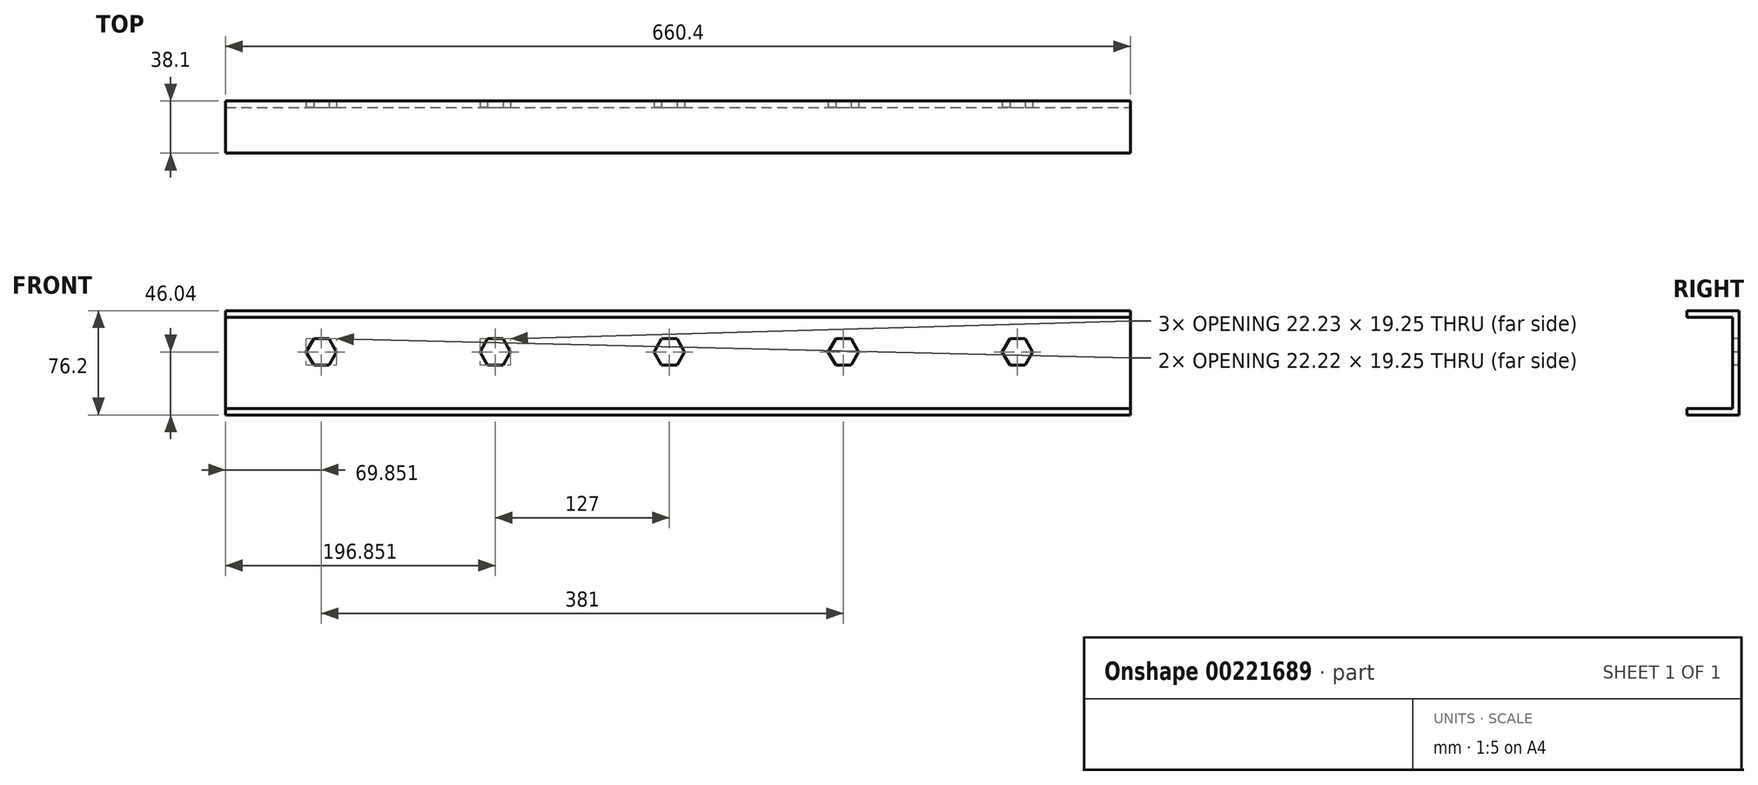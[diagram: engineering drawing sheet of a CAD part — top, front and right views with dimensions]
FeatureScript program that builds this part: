
annotation { "Feature Type Name" : "Feature", "Feature Type Description" : "" }
export const myFeature = defineFeature(function(context is Context, id is Id, definition is map)
    precondition{}
    {
        {
            var Q0;
            Q0=qCreatedBy(makeId("Front.planeOp"),FACE);
            var sketch = newSketch(context, id + "F0", { "sketchPlane" : qUnion([Q0])});
            skLineSegment(sketch, "E0.bottom", {"start": v(-341.97, -48.15) * mm, "end": v(318.43, -48.15) * mm});
            skLineSegment(sketch, "E0.top", {"start": v(-341.97, 28.05) * mm, "end": v(318.43, 28.05) * mm});
            skLineSegment(sketch, "E0.left", {"start": v(-341.97, -48.15) * mm, "end": v(-341.97, 28.05) * mm});
            skLineSegment(sketch, "E0.right", {"start": v(318.43, -48.15) * mm, "end": v(318.43, 28.05) * mm});
            skSolve(sketch);
        }
        {
            var Q0;
            Q0 = qSketchRegion(id + "F0", true);
            extrude(context, id + "F1", {"entities" : qUnion([Q0]), "oppositeDirection" : true, "depth" : 38.1 * mm});
        }
        {
            var Q0;
            Q0=makeQuery(id+"F1.opExtrude","CAP_FACE",FACE,{"disambiguationData":[OSD([sQuery(id+"F0.wireOp",EDGE,"E0.bottom"),sQuery(id+"F0.wireOp",EDGE,"E0.top"),sQuery(id+"F0.wireOp",EDGE,"E0.left"),sQuery(id+"F0.wireOp",EDGE,"E0.right")])],"isStart":true});
            var sketch = newSketch(context, id + "F2", { "sketchPlane" : qUnion([Q0])});
            skLineSegment(sketch, "E1.bottom", {"start": v(-341.97, -43.38) * mm, "end": v(318.43, -43.38) * mm});
            skLineSegment(sketch, "E1.top", {"start": v(-341.97, 23.3) * mm, "end": v(318.43, 23.3) * mm});
            skLineSegment(sketch, "E1.left", {"start": v(-341.97, -43.38) * mm, "end": v(-341.97, 23.3) * mm});
            skLineSegment(sketch, "E1.right", {"start": v(318.43, -43.38) * mm, "end": v(318.43, 23.3) * mm});
            skSolve(sketch);
        }
        {
            var Q0;
            Q0 = qSketchRegion(id + "F2", true);
            extrude(context, id + "F3", {"entities" : qUnion([Q0]), "operationType" : NewBodyOperationType.REMOVE, "oppositeDirection" : true, "depth" : 33.34 * mm});
        }
        {
            var Q0;
            Q0=makeQuery(id+"F3.boolean.opBoolean","COPY",FACE,{"derivedFrom":makeQuery(id+"F3.opExtrude","CAP_FACE",FACE,{"disambiguationData":[OSD([sQuery(id+"F2.wireOp",EDGE,"E1.bottom"),sQuery(id+"F2.wireOp",EDGE,"E1.top"),sQuery(id+"F2.wireOp",EDGE,"E1.left"),sQuery(id+"F2.wireOp",EDGE,"E1.right")])],"isStart":false})});
            var sketch = newSketch(context, id + "F4", { "sketchPlane" : qUnion([Q0])});
            skCircle(sketch, "E2.cCircle", {"center": v(-272.12, -2.1) * mm, "radius": 9.62 * mm, "construction": true});
            skLineSegment(sketch, "E2.0", {"start": v(-283.23, -2.1) * mm, "end": v(-277.68, 7.51) * mm});
            skLineSegment(sketch, "E2.1", {"start": v(-277.68, 7.51) * mm, "end": v(-266.56, 7.51) * mm});
            skLineSegment(sketch, "E2.2", {"start": v(-266.56, 7.51) * mm, "end": v(-261, -2.1) * mm});
            skLineSegment(sketch, "E2.3", {"start": v(-261, -2.1) * mm, "end": v(-266.56, -11.73) * mm});
            skLineSegment(sketch, "E2.4", {"start": v(-266.56, -11.73) * mm, "end": v(-277.68, -11.73) * mm});
            skLineSegment(sketch, "E2.5", {"start": v(-277.68, -11.73) * mm, "end": v(-283.23, -2.1) * mm});
            skPoint(sketch, "E2.0.midPoint", {"position": v(-280.45, 2.7) * mm});
            skCircle(sketch, "E3.1.0.0", {"center": v(-145.12, -2.1) * mm, "radius": 9.62 * mm, "construction": true});
            skLineSegment(sketch, "E3.1.0.1", {"start": v(-156.23, -2.1) * mm, "end": v(-150.68, 7.51) * mm});
            skLineSegment(sketch, "E3.1.0.2", {"start": v(-150.68, -11.73) * mm, "end": v(-156.23, -2.1) * mm});
            skLineSegment(sketch, "E3.1.0.3", {"start": v(-139.56, -11.73) * mm, "end": v(-150.68, -11.73) * mm});
            skLineSegment(sketch, "E3.1.0.4", {"start": v(-134, -2.1) * mm, "end": v(-139.56, -11.73) * mm});
            skLineSegment(sketch, "E3.1.0.5", {"start": v(-139.56, 7.51) * mm, "end": v(-134, -2.1) * mm});
            skLineSegment(sketch, "E3.1.0.6", {"start": v(-150.68, 7.51) * mm, "end": v(-139.56, 7.51) * mm});
            skCircle(sketch, "E3.2.0.0", {"center": v(-18.12, -2.1) * mm, "radius": 9.62 * mm, "construction": true});
            skLineSegment(sketch, "E3.2.0.1", {"start": v(-29.23, -2.1) * mm, "end": v(-23.68, 7.51) * mm});
            skLineSegment(sketch, "E3.2.0.2", {"start": v(-23.68, -11.73) * mm, "end": v(-29.23, -2.1) * mm});
            skLineSegment(sketch, "E3.2.0.3", {"start": v(-12.56, -11.73) * mm, "end": v(-23.68, -11.73) * mm});
            skLineSegment(sketch, "E3.2.0.4", {"start": v(-7, -2.1) * mm, "end": v(-12.56, -11.73) * mm});
            skLineSegment(sketch, "E3.2.0.5", {"start": v(-12.56, 7.51) * mm, "end": v(-7, -2.1) * mm});
            skLineSegment(sketch, "E3.2.0.6", {"start": v(-23.68, 7.51) * mm, "end": v(-12.56, 7.51) * mm});
            skCircle(sketch, "E3.3.0.0", {"center": v(108.88, -2.1) * mm, "radius": 9.62 * mm, "construction": true});
            skLineSegment(sketch, "E3.3.0.1", {"start": v(97.77, -2.1) * mm, "end": v(103.32, 7.51) * mm});
            skLineSegment(sketch, "E3.3.0.2", {"start": v(103.32, -11.73) * mm, "end": v(97.77, -2.1) * mm});
            skLineSegment(sketch, "E3.3.0.3", {"start": v(114.44, -11.73) * mm, "end": v(103.32, -11.73) * mm});
            skLineSegment(sketch, "E3.3.0.4", {"start": v(120, -2.1) * mm, "end": v(114.44, -11.73) * mm});
            skLineSegment(sketch, "E3.3.0.5", {"start": v(114.44, 7.51) * mm, "end": v(120, -2.1) * mm});
            skLineSegment(sketch, "E3.3.0.6", {"start": v(103.32, 7.51) * mm, "end": v(114.44, 7.51) * mm});
            skCircle(sketch, "E3.4.0.0", {"center": v(235.88, -2.1) * mm, "radius": 9.62 * mm, "construction": true});
            skLineSegment(sketch, "E3.4.0.1", {"start": v(224.77, -2.1) * mm, "end": v(230.32, 7.51) * mm});
            skLineSegment(sketch, "E3.4.0.2", {"start": v(230.32, -11.73) * mm, "end": v(224.77, -2.1) * mm});
            skLineSegment(sketch, "E3.4.0.3", {"start": v(241.44, -11.73) * mm, "end": v(230.32, -11.73) * mm});
            skLineSegment(sketch, "E3.4.0.4", {"start": v(247, -2.1) * mm, "end": v(241.44, -11.73) * mm});
            skLineSegment(sketch, "E3.4.0.5", {"start": v(241.44, 7.51) * mm, "end": v(247, -2.1) * mm});
            skLineSegment(sketch, "E3.4.0.6", {"start": v(230.32, 7.51) * mm, "end": v(241.44, 7.51) * mm});
            skLineSegment(sketch, "E3.direction1", {"start": v(-272.12, -2.1) * mm, "end": v(-145.12, -2.1) * mm, "construction": true});
            skSolve(sketch);
        }
        {
            var Q0;
            Q0 = qSketchRegion(id + "F4", true);
            extrude(context, id + "F5", {"entities" : qUnion([Q0]), "operationType" : NewBodyOperationType.REMOVE, "oppositeDirection" : true, "depth" : 25.4 * mm});
        }
    });
